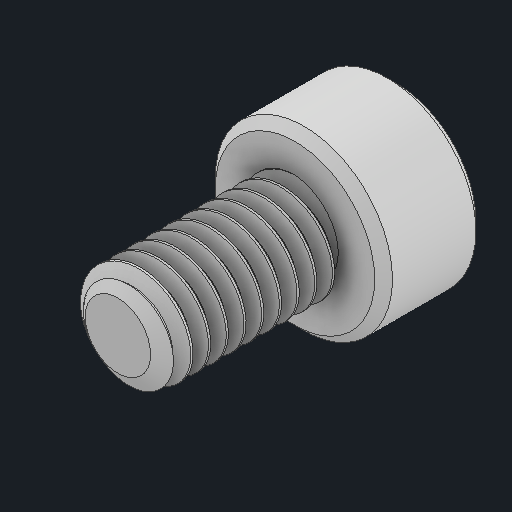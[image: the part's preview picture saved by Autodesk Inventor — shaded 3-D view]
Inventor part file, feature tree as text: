
AUTODESK INVENTOR PART (.ipt)
format: ipt  version: 2023 (Build 270158000, 158)  size: 432,128 bytes
history: native  units: in
note: dims shown in document units (in); Inventor stores cm internally (conversion verified against a paired STEP export)
features: chamfer x1
ambient origin geometry x8: Origin, YZ Plane, XZ Plane, XY Plane, X Axis, Y Axis, Z Axis, Center Point
bodies: Solid1 (feature_tree)
feature tree (1):
  chamfer  "Chamfer1"  [1 undecoded]
note: 1 required parameter value undecoded (feature->parameter linkage not recoverable at this tier; creation-order binding heuristic only, values carry confidence <= 0.55)
